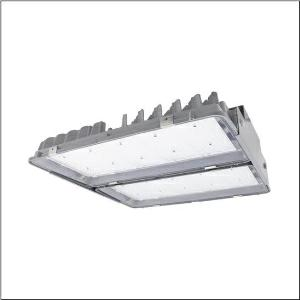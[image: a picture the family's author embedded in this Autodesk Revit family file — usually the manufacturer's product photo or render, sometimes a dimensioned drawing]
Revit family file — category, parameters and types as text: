
# Revit family: highbay_11xtreme_51hf62db4tma
name_source: partatom
category: Lighting Fixtures
units: mm (PartAtom-declared; Revit-internal decimal feet)

## family parameters
Cut with Voids When Loaded = No
Host = Face
Light Source = No
Part Type = Normal
Room Calculation Point = No
Round Connector Dimension = Use Diameter
Shared = No

## types (1)
- --- (1 x LED, 54000 lm, 285.7 W, 4000K)
    Apparent Load = 286 VA
    CIE Flux Codes = 84 96 100 100 100
    Color Rendering = 80
    Color Temperature = 4000K
    Default Elevation = 1800 mm
    Description = Highbay 11Xtreme, LED high bay luminaire, primary light control with lens, of PMMA, primary optical cover: cover, of toughened safety glass, light emission: direct distribution, primary light characteristic: symmetric, installation type: suspended mounting, surface-mounted, 2x LED module,for 1x 2x LED, rated luminous flux: 54.000lm, luminous efficacy: 189lm/W, light colour: 840, colour temperature: 4000K, with cable H07RN-F 5x 1.5mm², mains connection: 220..240V, AC, 50/60Hz, cable length: 1,5m, rated input power: 286W, luminaire housing, of diecast aluminium, coated, silver, length: 595mm, width: 560mm, height: 195mm, protection rating (complete): IP66, insulation class (complete): insulation class I (protective earthing), certification: CE, ENEC, UKCA, protection symbol: D, ball protection: ball impact resistant according to DIN VDE 0710 part 13 (with chain suspension), impact resistance: IK08, permissible operating ambient temperature: -25..+60°C, reducing of maximum allowable ambient temperature of 5°C with ceiling mounting, packaging unit: 1 piece
    Height = 157 mm
    Lamp = 1 x LED
    Lamp Light Flux = 54000 lm
    Lamp Power = 285.7 W
    Lamp count = 1
    Length = 593 mm
    Luminous efficacy = 189 lm/W
    Manufacturer = Siteco
    ModVariant = No
    Model = 51HF62DB4TMA
    Mounting Place = Ceiling
    Mounting Type = Pendant
    Number of Poles = 1
    OnlyDefault = Yes
    Power Factor = 1
    Product Name = Highbay 11Xtreme
    Product group = LED high bay luminaire
    ProductGroupID = 903
    Protection Class = Protection class I
    Protection Degree = IP 66
    RLX_Detail_Level = 1
    RLX_Emergency_Light_Flux = 0 lm
    RLX_Emergency_Type = 0
    RLX_Emergency_Type_DB = No
    RlxData = <blob elided: 34285 chars, md5=6aa2a27a>
    Socket = socket
    Standby Power = 0 W
    System Light Flux = 54000 lm
    System Power = 286 W
    Type Comments = factory setting: luminous flux: 100 % | dim-lin: 254 | 970 mA
    Type Image = l_1258340.jpg
    URL = http://relux.com
    VarID = @adj_035503
    Voltage = 0 V
    Weight = 0.00 kg
    Width = 568 mm

## geometry (parser evidence)
native form markers: Blend x4, Sweep x10
no freeform markers — native parametric forms only
